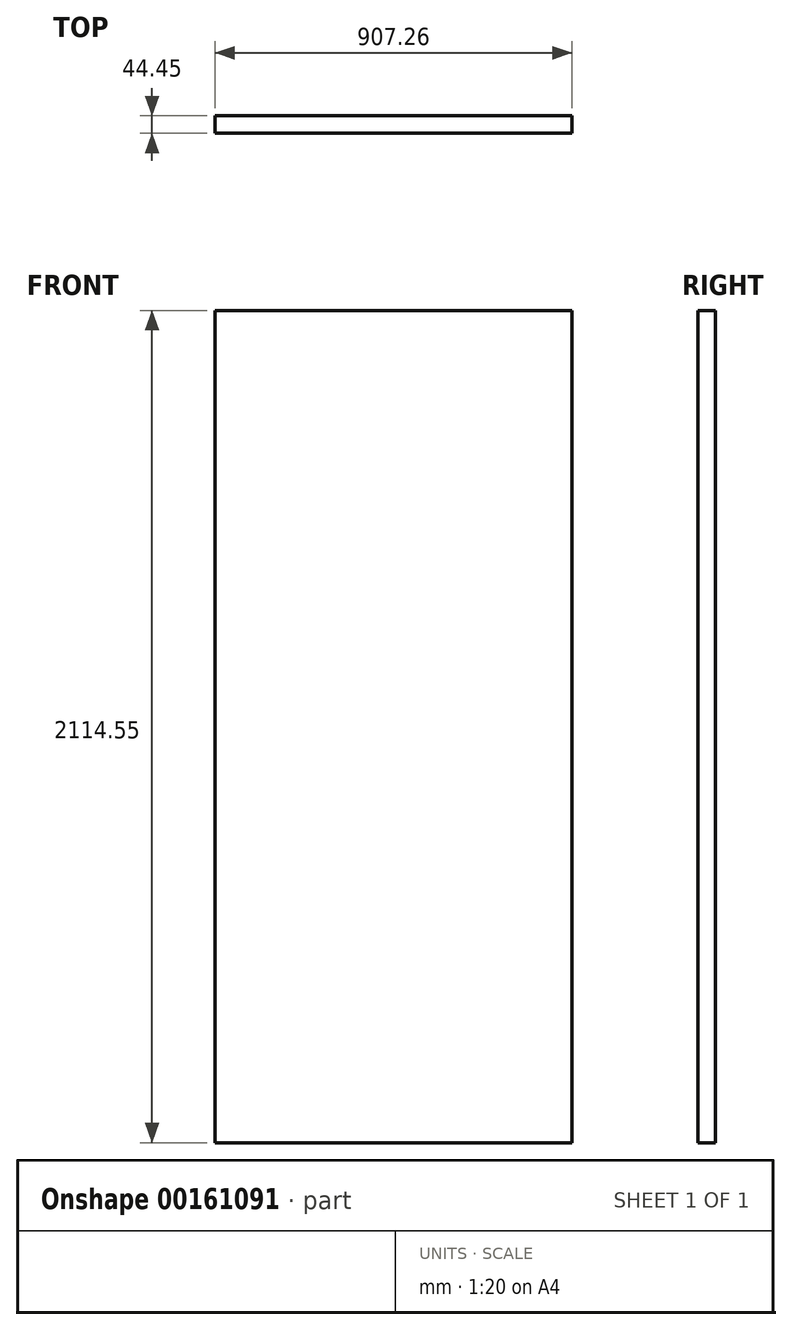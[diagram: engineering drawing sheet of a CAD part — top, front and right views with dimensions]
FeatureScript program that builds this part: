
annotation { "Feature Type Name" : "Feature", "Feature Type Description" : "" }
export const myFeature = defineFeature(function(context is Context, id is Id, definition is map)
    precondition{}
    {
        {
            var Q0;
            Q0=qCreatedBy(makeId("Top.planeOp"),FACE);
            var sketch = newSketch(context, id + "F0", { "sketchPlane" : qUnion([Q0])});
            skLineSegment(sketch, "E0.bottom", {"start": v(0, 0) * mm, "end": v(-907.26, 0) * mm});
            skLineSegment(sketch, "E0.top", {"start": v(0, 44.45) * mm, "end": v(-907.26, 44.45) * mm});
            skLineSegment(sketch, "E0.left", {"start": v(0, 0) * mm, "end": v(0, 44.45) * mm});
            skLineSegment(sketch, "E0.right", {"start": v(-907.26, 0) * mm, "end": v(-907.26, 44.45) * mm});
            skSolve(sketch);
        }
        {
            var Q0;
            Q0=qSketchRegion(id+"F0",true);
            extrude(context, id + "F1", {"entities" : qUnion([Q0]), "depth" : 2114.55 * mm});
        }
    });
